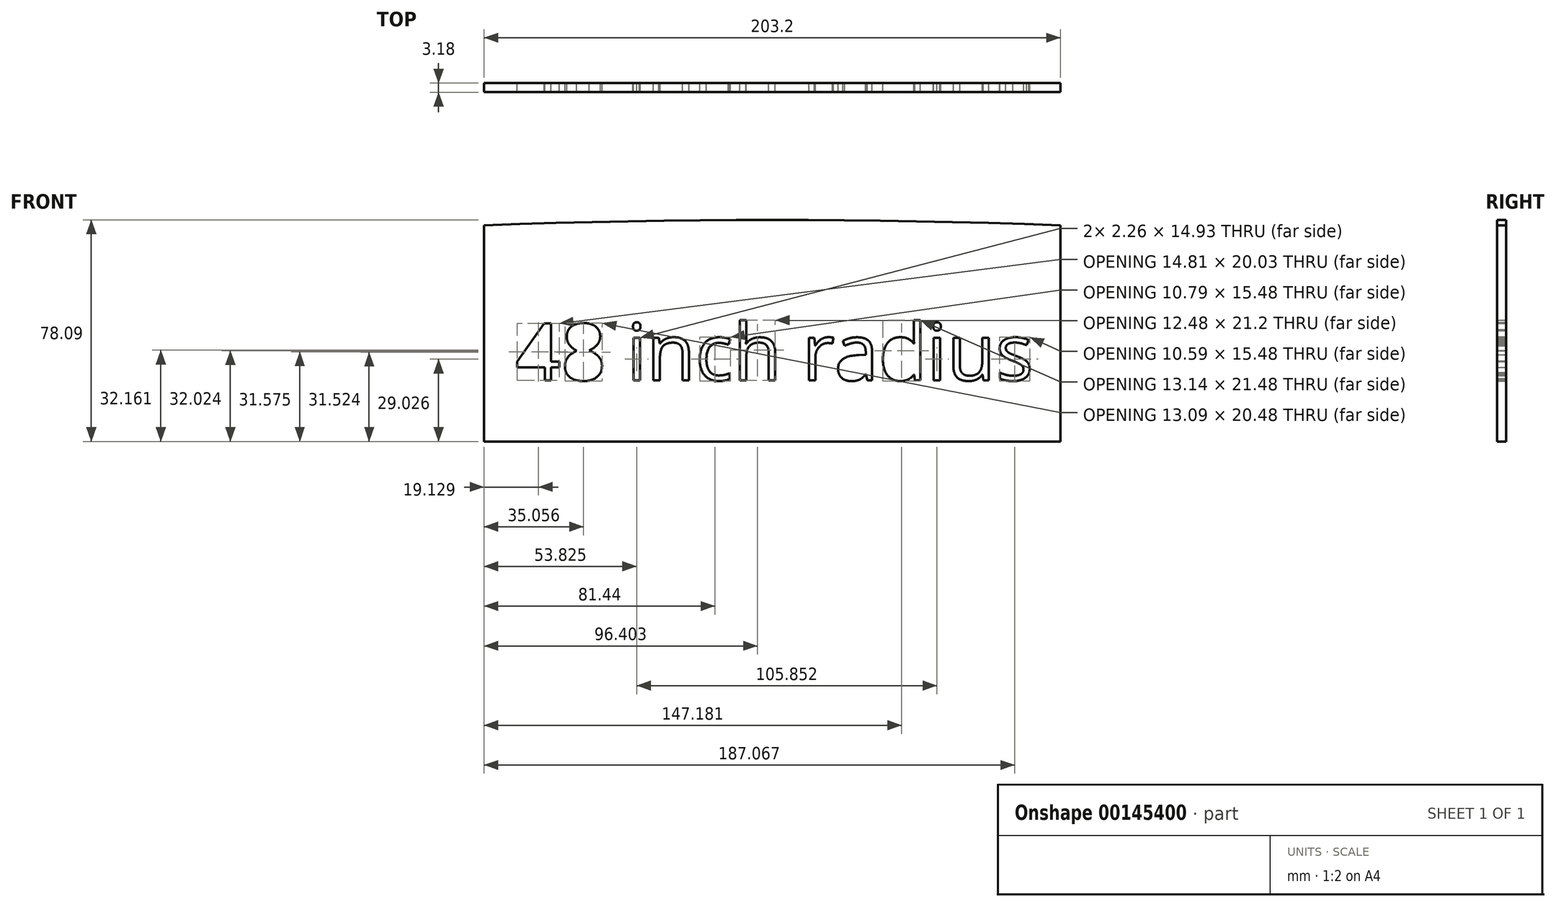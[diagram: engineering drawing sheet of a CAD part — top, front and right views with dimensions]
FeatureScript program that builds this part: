
annotation { "Feature Type Name" : "Feature", "Feature Type Description" : "" }
export const myFeature = defineFeature(function(context is Context, id is Id, definition is map)
    precondition{}
    {
        {
            var Q0;
            Q0=qCreatedBy(makeId("Front.planeOp"),FACE);
            var sketch = newSketch(context, id + "F0", { "sketchPlane" : qUnion([Q0])});
            skArc(sketch, "E0", {"start": v(101.6, 2733.19) * mm, "mid": v(0, 2735.08) * mm, "end": v(-101.6, 2733.19) * mm});
            skLineSegment(sketch, "E1.bottom", {"start": v(101.6, 2656.99) * mm, "end": v(-101.6, 2656.99) * mm});
            skLineSegment(sketch, "E1.left", {"start": v(101.6, 2656.99) * mm, "end": v(101.6, 2733.19) * mm});
            skLineSegment(sketch, "E1.right", {"start": v(-101.6, 2656.99) * mm, "end": v(-101.6, 2733.19) * mm});
            skPoint(sketch, "E1.middle", {"position": v(92.56, 2678.55) * mm});
            skPoint(sketch, "E2.orphan", {"position": v(-101.6, 2724.72) * mm});
            skPoint(sketch, "E3.orphan", {"position": v(101.6, 2724.72) * mm});
            skText(sketch, "E4", { "text": "48 inch radius", "fontName": "OpenSans-Regular.ttf"});
            const initialGuessF0  = {"E4": [-0.09046, 2.67855, 1, 0, 0.02009]};
            skSetInitialGuess(sketch, initialGuessF0);
            skSolve(sketch);
        }
        {
            var Q0;
            Q0=makeQuery(id+"F0.imprint","IMPRINT",FACE,{"disambiguationData":[TD([[makeQuery(id+"F0.imprint","IMPRINT",EDGE,{"derivedFrom":sQuery(id+"F0.wireOp",EDGE,"E0")}),1.0]])]});
            extrude(context, id + "F1", {"entities" : qUnion([Q0]), "depth" : 3.17 * mm});
        }
    });
